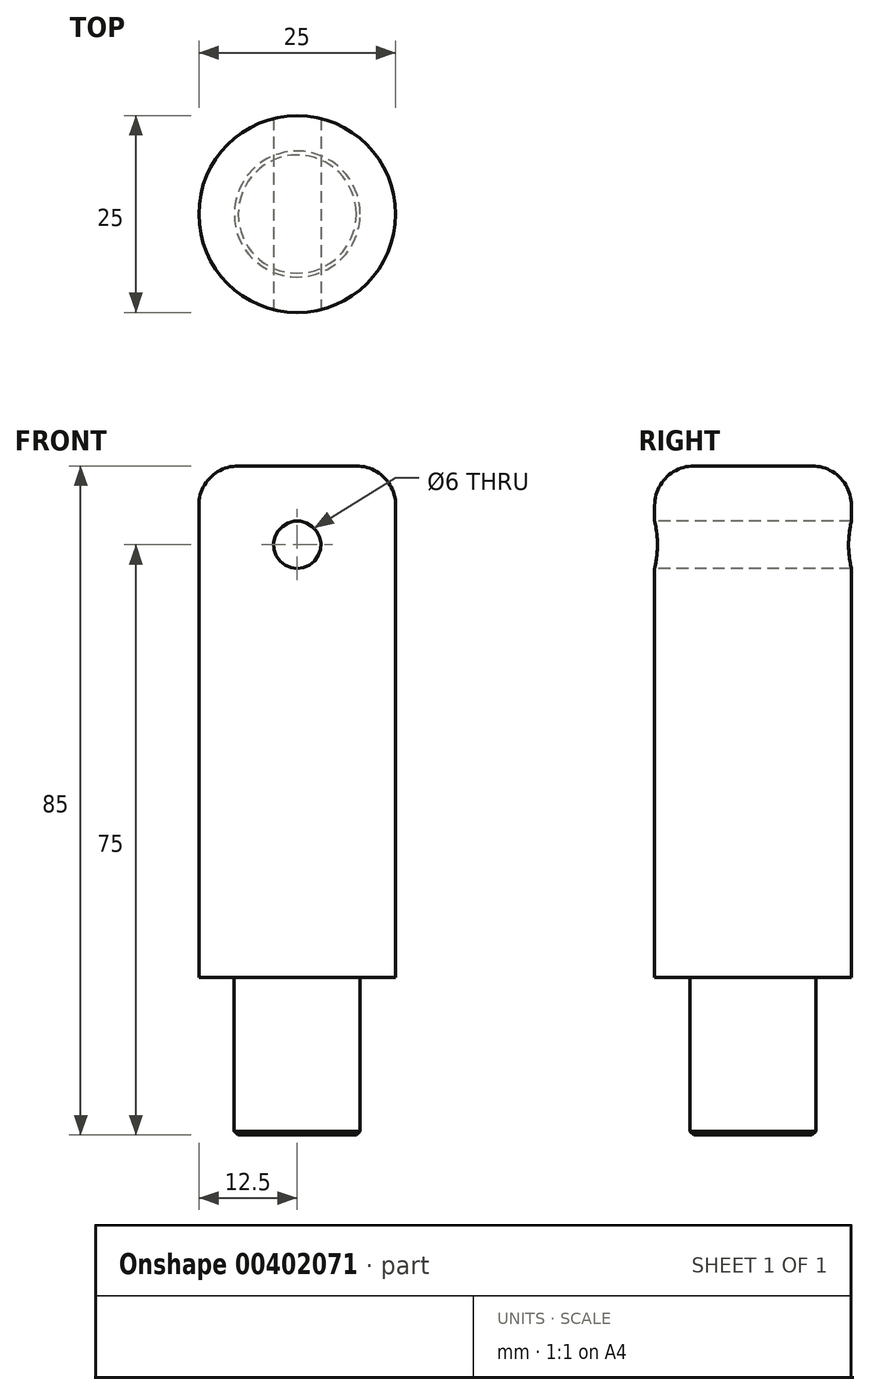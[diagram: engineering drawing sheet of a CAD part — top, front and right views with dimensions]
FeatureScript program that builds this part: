
annotation { "Feature Type Name" : "Feature", "Feature Type Description" : "" }
export const myFeature = defineFeature(function(context is Context, id is Id, definition is map)
    precondition{}
    {
        {
            var Q0;
            Q0=qCreatedBy(makeId("Top.planeOp"),FACE);
            var sketch = newSketch(context, id + "F0", { "sketchPlane" : qUnion([Q0])});
            skCircle(sketch, "E0", {"center": v(0, 0) * mm, "radius": 12.5 * mm});
            skSolve(sketch);
        }
        {
            var Q0;
            Q0=qSketchRegion(id+"F0",true);
            extrude(context, id + "F1", {"entities" : qUnion([Q0]), "depth" : 65 * mm});
        }
        {
            var Q0;
            Q0=makeQuery(id+"F1.opExtrude","CAP_EDGE",EDGE,{"disambiguationData":[OSD([sQuery(id+"F0.wireOp",EDGE,"E0")])],"isStart":false});
            fillet(context, id + "F2", {"entities" : qUnion([Q0]), "radius" : 5 * mm, "tangentPropagation" : true, "allowEdgeOverflow" : false});
        }
        {
            var Q0;
            Q0=makeQuery(id+"F1.opExtrude","CAP_FACE",FACE,{"disambiguationData":[OSD([sQuery(id+"F0.wireOp",EDGE,"E0")])],"isStart":true});
            var sketch = newSketch(context, id + "F3", { "sketchPlane" : qUnion([Q0])});
            skCircle(sketch, "E1", {"center": v(0, 0) * mm, "radius": 8 * mm});
            skSolve(sketch);
        }
        {
            var Q0;
            Q0=qSketchRegion(id+"F3",true);
            extrude(context, id + "F4", {"entities" : qUnion([Q0]), "operationType" : NewBodyOperationType.ADD, "depth" : 20 * mm});
        }
        {
            var Q0;
            Q0=makeQuery(id+"F4.opExtrude","CAP_EDGE",EDGE,{"disambiguationData":[OSD([sQuery(id+"F3.wireOp",EDGE,"E1")])],"isStart":false});
            var Q1;
            Q1=makeQuery(id+"F4.opExtrude","CAP_EDGE",EDGE,{"disambiguationData":[OSD([sQuery(id+"F3.wireOp",EDGE,"E1")])],"isStart":true});
            chamfer(context, id + "F5", {"entities" : qUnion([Q0, Q1]), "width" : 0.5 * mm, "tangentPropagation" : true});
        }
        {
            var Q0;
            Q0=qCreatedBy(makeId("Front.planeOp"),FACE);
            var sketch = newSketch(context, id + "F6", { "sketchPlane" : qUnion([Q0])});
            skCircle(sketch, "E2", {"center": v(0, 55) * mm, "radius": 3 * mm});
            skSolve(sketch);
        }
        {
            var Q0;
            Q0 = qSketchRegion(id + "F6", true);
            extrude(context, id + "F7", {"entities" : qUnion([Q0]), "operationType" : NewBodyOperationType.REMOVE, "endBound" : BoundingType.SYMMETRIC, "oppositeDirection" : true, "depth" : 40 * mm});
        }
    });
